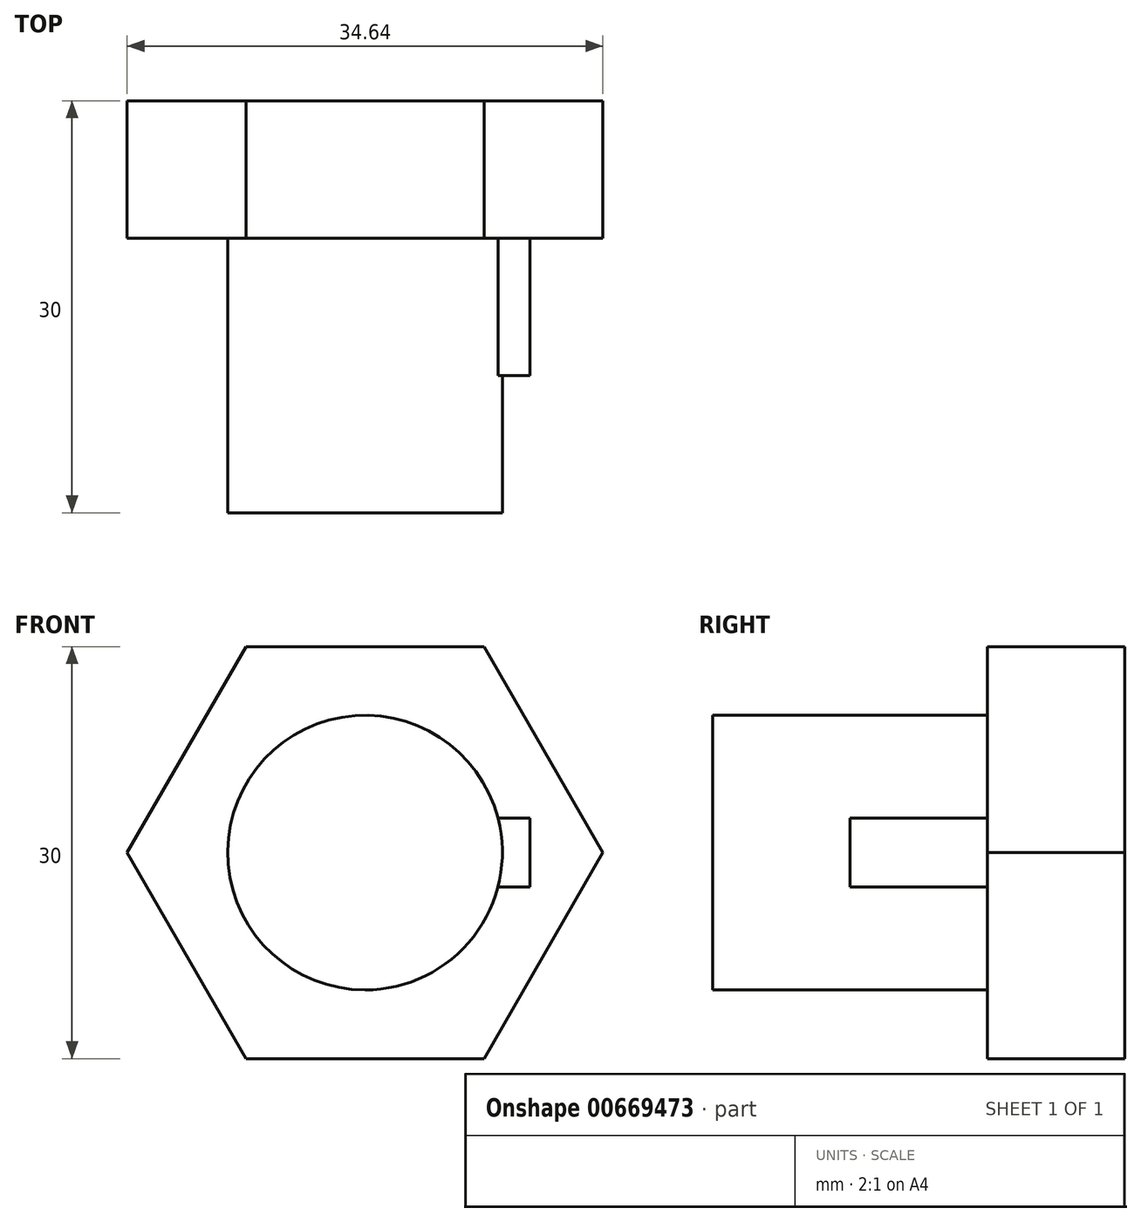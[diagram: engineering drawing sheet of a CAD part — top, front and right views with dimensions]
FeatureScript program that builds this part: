
annotation { "Feature Type Name" : "Feature", "Feature Type Description" : "" }
export const myFeature = defineFeature(function(context is Context, id is Id, definition is map)
    precondition{}
    {
        {
            var Q0;
            Q0=qCreatedBy(makeId("Front.planeOp"),FACE);
            var sketch = newSketch(context, id + "F0", { "sketchPlane" : qUnion([Q0])});
            skCircle(sketch, "E0.cCircle", {"center": v(0, 0) * mm, "radius": 15 * mm, "construction": true});
            skLineSegment(sketch, "E0.0", {"start": v(8.66, -15) * mm, "end": v(-8.66, -15) * mm});
            skLineSegment(sketch, "E0.1", {"start": v(-8.66, -15) * mm, "end": v(-17.32, 0) * mm});
            skLineSegment(sketch, "E0.2", {"start": v(-17.32, 0) * mm, "end": v(-8.66, 15) * mm});
            skLineSegment(sketch, "E0.3", {"start": v(-8.66, 15) * mm, "end": v(8.66, 15) * mm});
            skLineSegment(sketch, "E0.4", {"start": v(8.66, 15) * mm, "end": v(17.32, 0) * mm});
            skLineSegment(sketch, "E0.5", {"start": v(17.32, 0) * mm, "end": v(8.66, -15) * mm});
            skPoint(sketch, "E0.0.midPoint", {"position": v(0, -15) * mm});
            skCircle(sketch, "E1", {"center": v(0, 0) * mm, "radius": 10 * mm});
            skLineSegment(sketch, "E2.bottom", {"start": v(9.68, 2.5) * mm, "end": v(12, 2.5) * mm});
            skLineSegment(sketch, "E2.top", {"start": v(9.68, -2.5) * mm, "end": v(12, -2.5) * mm});
            skLineSegment(sketch, "E2.right", {"start": v(12, 2.5) * mm, "end": v(12, -2.5) * mm});
            skPoint(sketch, "E2.middle", {"position": v(10, 0) * mm});
            skPoint(sketch, "E2.left.start.orphan", {"position": v(8, 2.5) * mm});
            skPoint(sketch, "E3.orphan", {"position": v(8, -2.5) * mm});
            skSolve(sketch);
        }
        {
            var Q0;
            {var subQ0=sQuery(id+"F0.wireOp",EDGE,"E1");var subQ1=makeQuery(id+"F0.imprint","INTERSECT",VERTEX,{"derivedFrom":[subQ0,sQuery(id+"F0.wireOp",EDGE,"E2.bottom")]});Q0=makeQuery(id+"F0.imprint","IMPRINT",FACE,{"disambiguationData":[TD([[makeQuery(id+"F0.imprint","IMPRINT",EDGE,{"disambiguationData":[TD([[subQ1,-1.0]])],"derivedFrom":subQ0}),1.0]])]});}
            extrude(context, id + "F1", {"entities" : qUnion([Q0]), "depth" : 30 * mm, "offsetDistance" : 25 * mm});
        }
        {
            var Q0;
            Q0=makeQuery(id+"F0.imprint","IMPRINT",FACE,{"disambiguationData":[TD([[makeQuery(id+"F0.imprint","IMPRINT",EDGE,{"derivedFrom":sQuery(id+"F0.wireOp",EDGE,"E0.0")}),-1.0]])]});
            var Q1;
            {var subQ0=sQuery(id+"F0.wireOp",EDGE,"E2.bottom");Q1=makeQuery(id+"F0.imprint","IMPRINT",FACE,{"disambiguationData":[TD([[makeQuery(id+"F0.imprint","IMPRINT",EDGE,{"derivedFrom":subQ0}),-1.0]])]});}
            var Q2;
            {var subQ0=sQuery(id+"F0.wireOp",EDGE,"E1");var subQ1=makeQuery(id+"F0.imprint","INTERSECT",VERTEX,{"derivedFrom":[subQ0,sQuery(id+"F0.wireOp",EDGE,"E2.bottom")]});Q2=makeQuery(id+"F0.imprint","IMPRINT",FACE,{"disambiguationData":[TD([[makeQuery(id+"F0.imprint","IMPRINT",EDGE,{"disambiguationData":[TD([[subQ1,-1.0]])],"derivedFrom":subQ0}),1.0]])]});}
            extrude(context, id + "F2", {"entities" : qUnion([Q0, Q1, Q2]), "operationType" : NewBodyOperationType.ADD, "depth" : 10 * mm, "offsetDistance" : 25 * mm});
        }
        {
            var Q0;
            {var subQ0=sQuery(id+"F0.wireOp",EDGE,"E2.bottom");Q0=makeQuery(id+"F0.imprint","IMPRINT",FACE,{"disambiguationData":[TD([[makeQuery(id+"F0.imprint","IMPRINT",EDGE,{"derivedFrom":subQ0}),-1.0]])]});}
            extrude(context, id + "F3", {"entities" : qUnion([Q0]), "operationType" : NewBodyOperationType.ADD, "depth" : 20 * mm, "offsetDistance" : 25 * mm});
        }
    });
